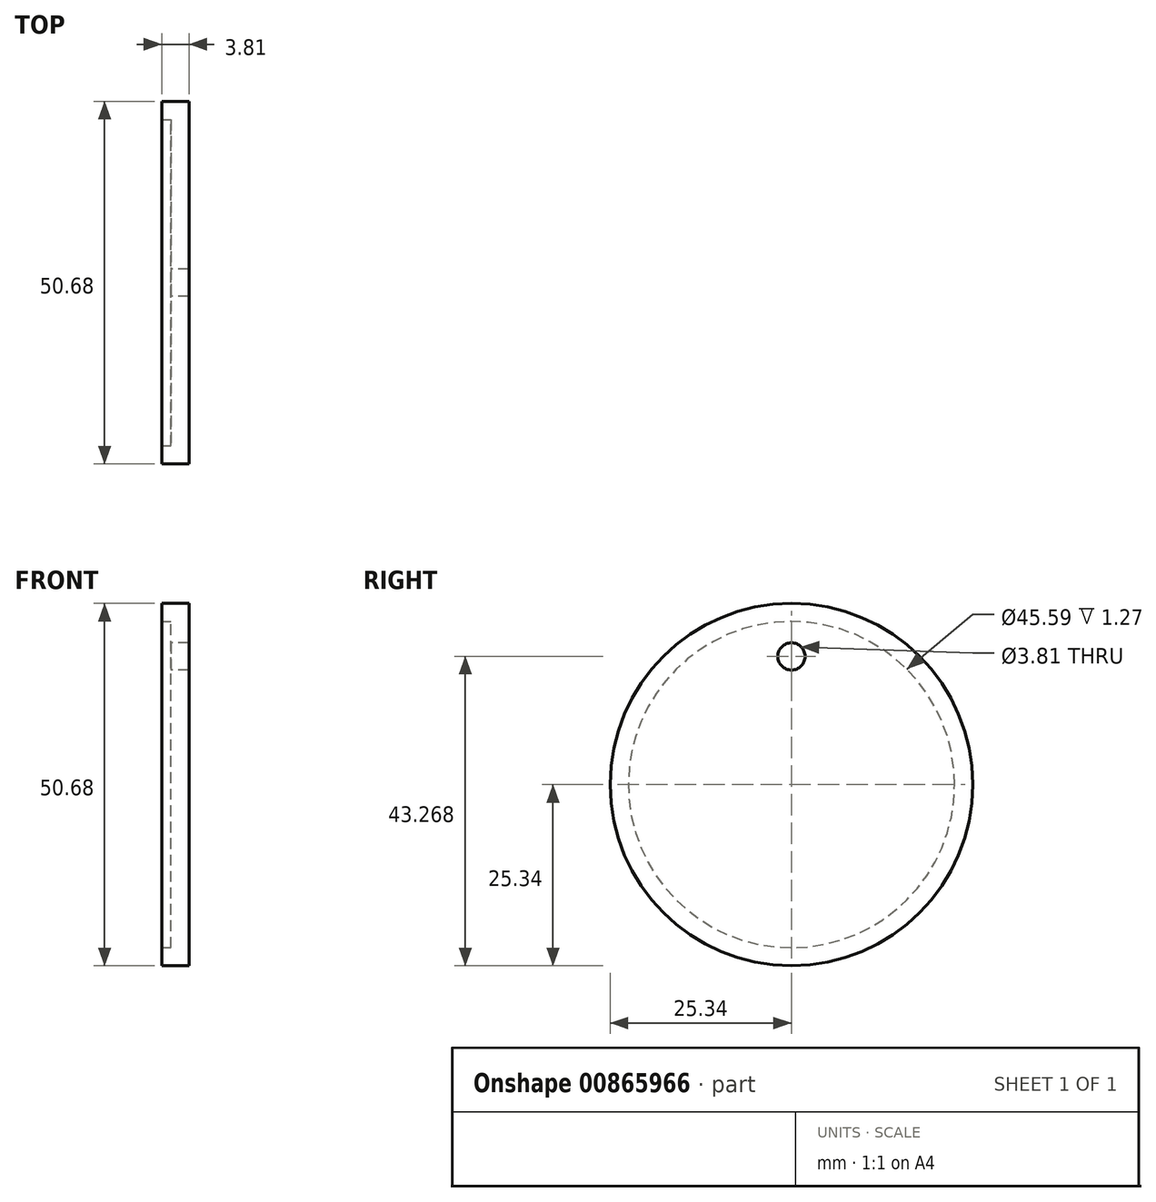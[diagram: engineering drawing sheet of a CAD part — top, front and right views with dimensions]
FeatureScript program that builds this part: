
annotation { "Feature Type Name" : "Feature", "Feature Type Description" : "" }
export const myFeature = defineFeature(function(context is Context, id is Id, definition is map)
    precondition{}
    {
        {
            var Q0;
            Q0=qCreatedBy(makeId("Right.planeOp"),FACE);
            var sketch = newSketch(context, id + "F0", { "sketchPlane" : qUnion([Q0])});
            skCircle(sketch, "E0", {"center": v(0, -2.2) * mm, "radius": 25.34 * mm});
            skSolve(sketch);
        }
        {
            var Q0;
            Q0=makeQuery(id+"F0.imprint","IMPRINT",FACE,{"disambiguationData":[TD([[makeQuery(id+"F0.imprint","IMPRINT",EDGE,{"derivedFrom":sQuery(id+"F0.wireOp",EDGE,"E0")}),1.0]])]});
            extrude(context, id + "F1", {"entities" : qUnion([Q0]), "oppositeDirection" : true, "depth" : 3.8 * mm, "offsetDistance" : 25.4 * mm});
        }
        {
            var Q0;
            Q0=makeQuery(id+"F1.opExtrude","CAP_FACE",FACE,{"disambiguationData":[OSD([sQuery(id+"F0.wireOp",EDGE,"E0")])],"isStart":false});
            shell(context, id + "F2", {"entities" : qUnion([Q0]), "thickness" : 2.54 * mm});
        }
        {
            var Q0;
            {var subQ0=sQuery(id+"F0.wireOp",EDGE,"E0");Q0=makeQuery(id+"F2.opShell","OFFSET_FACE",FACE,{"disambiguationData":[OSD([subQ0]),TDD([makeQuery(id+"F1.opExtrude","CAP_FACE",FACE,{"disambiguationData":[OSD([subQ0])],"isStart":true})])]});}
            var sketch = newSketch(context, id + "F3", { "sketchPlane" : qUnion([Q0])});
            skCircle(sketch, "E1", {"center": v(0, 15.74) * mm, "radius": 2.57 * mm});
            skSolve(sketch);
        }
        {
            var Q0;
            Q0=sQuery(id+"F3.wireOp",VERTEX,"E1.center");
            var Q1;
            Q1=makeQuery(id+"F1.opExtrude","SWEPT_BODY",BODY,{"disambiguationData":[OSD([sQuery(id+"F0.wireOp",EDGE,"E0")])]});
            hole(context, id + "F4", {"style" : HoleStyle.SIMPLE, "endStyle" : HoleEndStyle.BLIND, "holeDiameter" : 3.8 * mm, "majorDiameter" : 6.35 * mm, "holeDepth" : 2.54 * mm, "isTappedThrough" : true, "tappedDepth" : 12.7 * mm, "tapClearance" : 3, "startFromSketch" : true, "locations" : qUnion([Q0]), "scope" : qUnion([Q1])});
        }
    });
